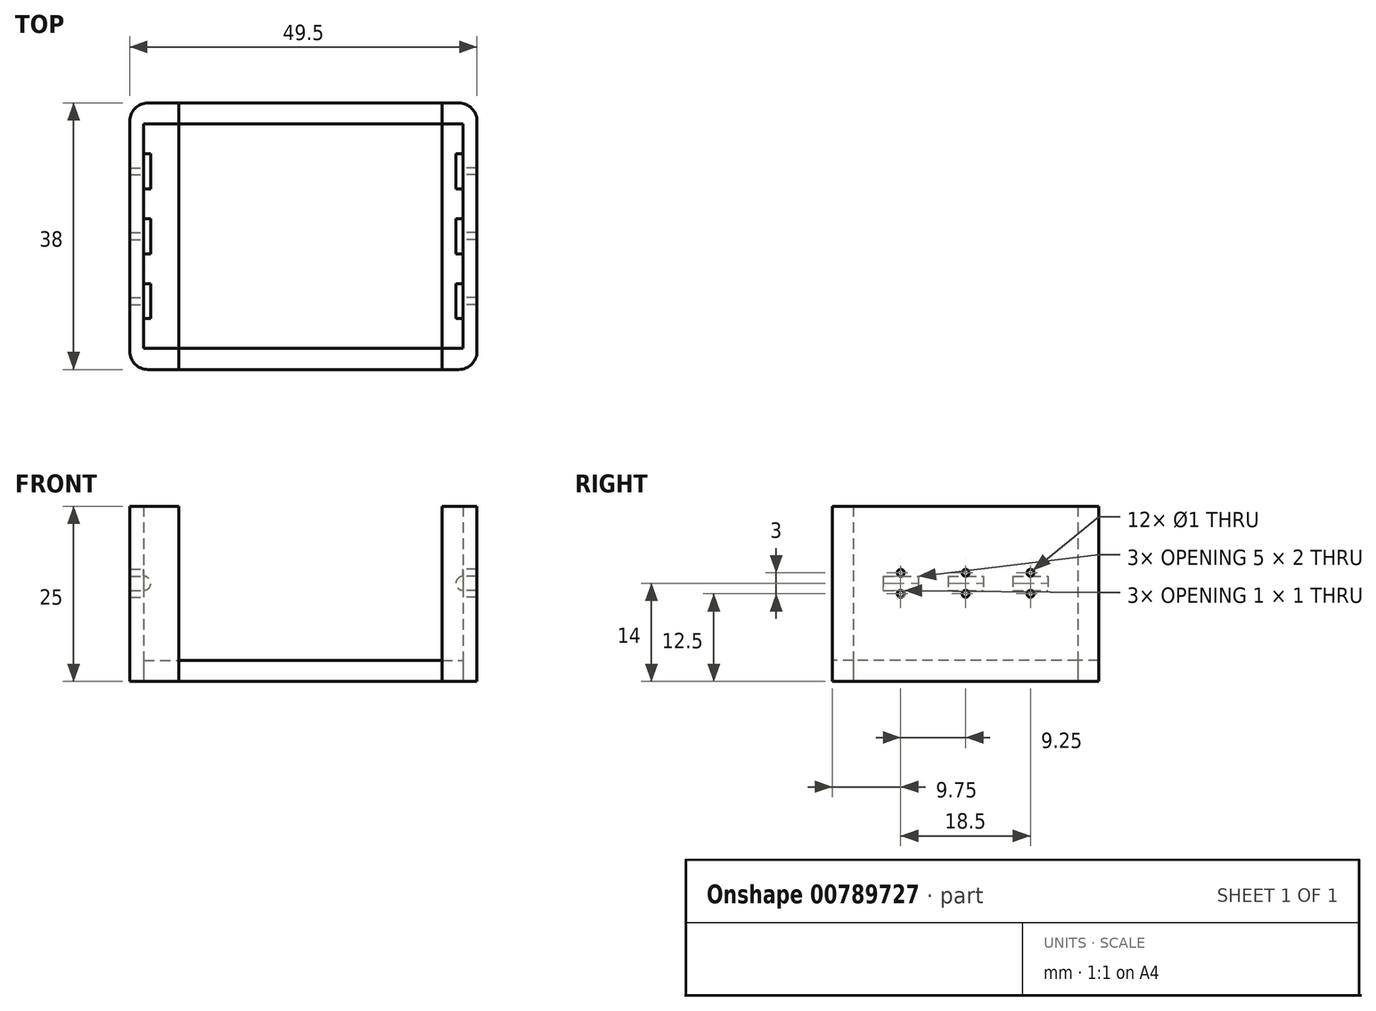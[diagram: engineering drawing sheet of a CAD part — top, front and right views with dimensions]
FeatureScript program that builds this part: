
annotation { "Feature Type Name" : "Feature", "Feature Type Description" : "" }
export const myFeature = defineFeature(function(context is Context, id is Id, definition is map)
    precondition{}
    {
        {
            var Q0;
            Q0=qCreatedBy(makeId("Top.planeOp"),FACE);
            var sketch = newSketch(context, id + "F0", { "sketchPlane" : qUnion([Q0])});
            skLineSegment(sketch, "E0.bottom", {"start": v(-24.75, 19) * mm, "end": v(24.75, 19) * mm});
            skLineSegment(sketch, "E0.top", {"start": v(-24.75, -19) * mm, "end": v(24.75, -19) * mm});
            skLineSegment(sketch, "E0.left", {"start": v(-24.75, 19) * mm, "end": v(-24.75, -19) * mm});
            skLineSegment(sketch, "E0.right", {"start": v(24.75, 19) * mm, "end": v(24.75, -19) * mm});
            skLineSegment(sketch, "E1.bottom", {"start": v(-24.75, 16) * mm, "end": v(24.75, 16) * mm});
            skLineSegment(sketch, "E1.top", {"start": v(-24.75, -16) * mm, "end": v(24.75, -16) * mm});
            skLineSegment(sketch, "E2", {"start": v(-22.75, 19) * mm, "end": v(-22.75, -19) * mm});
            skLineSegment(sketch, "E3", {"start": v(22.75, 19) * mm, "end": v(22.75, -19) * mm});
            skLineSegment(sketch, "E4", {"start": v(19.75, 19) * mm, "end": v(19.75, 16) * mm});
            skLineSegment(sketch, "E5", {"start": v(19.75, -16) * mm, "end": v(19.75, -19) * mm});
            skLineSegment(sketch, "E6", {"start": v(19.75, 16) * mm, "end": v(19.75, -16) * mm});
            skLineSegment(sketch, "E7", {"start": v(-17.75, 19) * mm, "end": v(-17.75, -19) * mm});
            skSolve(sketch);
        }
        {
            var Q0;
            {var subQ0=sQuery(id+"F0.wireOp",EDGE,"E1.bottom");var subQ1=sQuery(id+"F0.wireOp",EDGE,"E0.left");var subQ2=makeQuery(id+"F0.imprint","INTERSECT",VERTEX,{"derivedFrom":[subQ1,subQ0]});Q0=makeQuery(id+"F0.imprint","IMPRINT",FACE,{"disambiguationData":[TD([[makeQuery(id+"F0.imprint","IMPRINT",EDGE,{"disambiguationData":[TD([[subQ2,-1.0]])],"derivedFrom":subQ1}),1.0]])]});}
            var Q1;
            {var subQ0=sQuery(id+"F0.wireOp",EDGE,"E0.left");var subQ1=sQuery(id+"F0.wireOp",EDGE,"E0.bottom");var subQ2=makeQuery(id+"F0.imprint","INTERSECT",VERTEX,{"derivedFrom":[subQ1,subQ0]});Q1=makeQuery(id+"F0.imprint","IMPRINT",FACE,{"disambiguationData":[TD([[makeQuery(id+"F0.imprint","IMPRINT",EDGE,{"disambiguationData":[TD([[subQ2,-1.0]])],"derivedFrom":subQ1}),-1.0]])]});}
            var Q2;
            {var subQ3=sQuery(id+"F0.wireOp",EDGE,"JlUuSNjJ-N2WR-d7uv-6GBG-oXMLz9WUw5uQ");Q2=makeQuery(id+"F0.imprint","IMPRINT",FACE,{"disambiguationData":[TD([[makeQuery(id+"F0.imprint","IMPRINT",EDGE,{"derivedFrom":subQ3}),-1.0]])]});}
            var Q3;
            {var subQ3=sQuery(id+"F0.wireOp",EDGE,"6ny0mRPX-NTV9-We4M-mDfU-sZ6HuERO2ziz");Q3=makeQuery(id+"F0.imprint","IMPRINT",FACE,{"disambiguationData":[TD([[makeQuery(id+"F0.imprint","IMPRINT",EDGE,{"derivedFrom":subQ3}),-1.0]])]});}
            var Q4;
            {var subQ0=sQuery(id+"F0.wireOp",EDGE,"E0.left");var subQ1=sQuery(id+"F0.wireOp",EDGE,"E0.top");var subQ2=makeQuery(id+"F0.imprint","INTERSECT",VERTEX,{"derivedFrom":[subQ1,subQ0]});Q4=makeQuery(id+"F0.imprint","IMPRINT",FACE,{"disambiguationData":[TD([[makeQuery(id+"F0.imprint","IMPRINT",EDGE,{"disambiguationData":[TD([[subQ2,-1.0]])],"derivedFrom":subQ1}),1.0]])]});}
            var Q5;
            {var subQ3=sQuery(id+"F0.wireOp",EDGE,"E5");Q5=makeQuery(id+"F0.imprint","IMPRINT",FACE,{"disambiguationData":[TD([[makeQuery(id+"F0.imprint","IMPRINT",EDGE,{"derivedFrom":subQ3}),1.0]])]});}
            var Q6;
            {var subQ0=sQuery(id+"F0.wireOp",EDGE,"E0.right");var subQ1=sQuery(id+"F0.wireOp",EDGE,"E0.top");var subQ2=makeQuery(id+"F0.imprint","INTERSECT",VERTEX,{"derivedFrom":[subQ1,subQ0]});Q6=makeQuery(id+"F0.imprint","IMPRINT",FACE,{"disambiguationData":[TD([[makeQuery(id+"F0.imprint","IMPRINT",EDGE,{"disambiguationData":[TD([[subQ2,1.0]])],"derivedFrom":subQ1}),1.0]])]});}
            var Q7;
            {var subQ0=sQuery(id+"F0.wireOp",EDGE,"E1.bottom");var subQ1=sQuery(id+"F0.wireOp",EDGE,"E0.right");var subQ2=makeQuery(id+"F0.imprint","INTERSECT",VERTEX,{"derivedFrom":[subQ1,subQ0]});Q7=makeQuery(id+"F0.imprint","IMPRINT",FACE,{"disambiguationData":[TD([[makeQuery(id+"F0.imprint","IMPRINT",EDGE,{"disambiguationData":[TD([[subQ2,-1.0]])],"derivedFrom":subQ1}),-1.0]])]});}
            var Q8;
            {var subQ0=sQuery(id+"F0.wireOp",EDGE,"E0.right");var subQ1=sQuery(id+"F0.wireOp",EDGE,"E0.bottom");var subQ2=makeQuery(id+"F0.imprint","INTERSECT",VERTEX,{"derivedFrom":[subQ1,subQ0]});Q8=makeQuery(id+"F0.imprint","IMPRINT",FACE,{"disambiguationData":[TD([[makeQuery(id+"F0.imprint","IMPRINT",EDGE,{"disambiguationData":[TD([[subQ2,1.0]])],"derivedFrom":subQ1}),-1.0]])]});}
            var Q9;
            {var subQ3=sQuery(id+"F0.wireOp",EDGE,"E4");Q9=makeQuery(id+"F0.imprint","IMPRINT",FACE,{"disambiguationData":[TD([[makeQuery(id+"F0.imprint","IMPRINT",EDGE,{"derivedFrom":subQ3}),1.0]])]});}
            var Q10;
            {var subQ0=sQuery(id+"F0.wireOp",EDGE,"E2");var subQ1=sQuery(id+"F0.wireOp",EDGE,"E0.bottom");var subQ2=makeQuery(id+"F0.imprint","INTERSECT",VERTEX,{"derivedFrom":[subQ1,subQ0]});Q10=makeQuery(id+"F0.imprint","IMPRINT",FACE,{"disambiguationData":[TD([[makeQuery(id+"F0.imprint","IMPRINT",EDGE,{"disambiguationData":[TD([[subQ2,-1.0]])],"derivedFrom":subQ1}),-1.0]])]});}
            var Q11;
            {var subQ0=sQuery(id+"F0.wireOp",EDGE,"E2");var subQ1=sQuery(id+"F0.wireOp",EDGE,"E0.top");var subQ2=makeQuery(id+"F0.imprint","INTERSECT",VERTEX,{"derivedFrom":[subQ1,subQ0]});Q11=makeQuery(id+"F0.imprint","IMPRINT",FACE,{"disambiguationData":[TD([[makeQuery(id+"F0.imprint","IMPRINT",EDGE,{"disambiguationData":[TD([[subQ2,-1.0]])],"derivedFrom":subQ1}),1.0]])]});}
            extrude(context, id + "F1", {"entities" : qUnion([Q0, Q1, Q2, Q3, Q4, Q5, Q6, Q7, Q8, Q9, Q10, Q11]), "depth" : 25 * mm, "offsetDistance" : 25 * mm});
        }
        {
            var Q0;
            {var subQ0=sQuery(id+"F0.wireOp",EDGE,"JlUuSNjJ-N2WR-d7uv-6GBG-oXMLz9WUw5uQ");Q0=makeQuery(id+"F0.imprint","IMPRINT",FACE,{"disambiguationData":[TD([[makeQuery(id+"F0.imprint","IMPRINT",EDGE,{"derivedFrom":subQ0}),1.0]])]});}
            var Q1;
            {var subQ0=sQuery(id+"F0.wireOp",EDGE,"6ny0mRPX-NTV9-We4M-mDfU-sZ6HuERO2ziz");Q1=makeQuery(id+"F0.imprint","IMPRINT",FACE,{"disambiguationData":[TD([[makeQuery(id+"F0.imprint","IMPRINT",EDGE,{"derivedFrom":subQ0}),1.0]])]});}
            var Q2;
            {var subQ0=sQuery(id+"F0.wireOp",EDGE,"7H7hESgq-7wWA-rG7u-VLva-y2kTmdD04vns");Q2=makeQuery(id+"F0.imprint","IMPRINT",FACE,{"disambiguationData":[TD([[makeQuery(id+"F0.imprint","IMPRINT",EDGE,{"derivedFrom":subQ0}),1.0]])]});}
            var Q3;
            {var subQ0=sQuery(id+"F0.wireOp",EDGE,"E6");Q3=makeQuery(id+"F0.imprint","IMPRINT",FACE,{"disambiguationData":[TD([[makeQuery(id+"F0.imprint","IMPRINT",EDGE,{"derivedFrom":subQ0}),1.0]])]});}
            var Q4;
            {var subQ2=sQuery(id+"F0.wireOp",EDGE,"kKINSNnD-868z-kQwc-rezc-MHWNEOe5RiWT");Q4=makeQuery(id+"F0.imprint","IMPRINT",FACE,{"disambiguationData":[TD([[makeQuery(id+"F0.imprint","IMPRINT",EDGE,{"derivedFrom":subQ2}),-1.0]])]});}
            var Q5;
            {var subQ0=sQuery(id+"F0.wireOp",EDGE,"E4");Q5=makeQuery(id+"F0.imprint","IMPRINT",FACE,{"disambiguationData":[TD([[makeQuery(id+"F0.imprint","IMPRINT",EDGE,{"derivedFrom":subQ0}),-1.0]])]});}
            var Q6;
            {var subQ0=sQuery(id+"F0.wireOp",EDGE,"E2");var subQ1=sQuery(id+"F0.wireOp",EDGE,"E1.bottom");var subQ2=makeQuery(id+"F0.imprint","INTERSECT",VERTEX,{"derivedFrom":[subQ1,subQ0]});Q6=makeQuery(id+"F0.imprint","IMPRINT",FACE,{"disambiguationData":[TD([[makeQuery(id+"F0.imprint","IMPRINT",EDGE,{"disambiguationData":[TD([[subQ2,-1.0]])],"derivedFrom":subQ1}),-1.0]])]});}
            var Q7;
            {var subQ0=sQuery(id+"F0.wireOp",EDGE,"E5");Q7=makeQuery(id+"F0.imprint","IMPRINT",FACE,{"disambiguationData":[TD([[makeQuery(id+"F0.imprint","IMPRINT",EDGE,{"derivedFrom":subQ0}),-1.0]])]});}
            extrude(context, id + "F2", {"entities" : qUnion([Q0, Q1, Q2, Q3, Q4, Q5, Q6, Q7]), "depth" : 3 * mm, "offsetDistance" : 25 * mm});
        }
        {
            var Q0;
            Q0=makeQuery(id+"F1.opExtrude","SWEPT_EDGE",EDGE,{"disambiguationData":[OSD([sQuery(id+"F0.wireOp",EDGE,"E0.bottom"),sQuery(id+"F0.wireOp",EDGE,"E0.left")])]});
            var Q1;
            Q1=makeQuery(id+"F1.opExtrude","SWEPT_EDGE",EDGE,{"disambiguationData":[OSD([sQuery(id+"F0.wireOp",EDGE,"E0.bottom"),sQuery(id+"F0.wireOp",EDGE,"E0.right")])]});
            var Q2;
            Q2=makeQuery(id+"F1.opExtrude","SWEPT_EDGE",EDGE,{"disambiguationData":[OSD([sQuery(id+"F0.wireOp",EDGE,"E0.top"),sQuery(id+"F0.wireOp",EDGE,"E0.right")])]});
            var Q3;
            Q3=makeQuery(id+"F1.opExtrude","SWEPT_EDGE",EDGE,{"disambiguationData":[OSD([sQuery(id+"F0.wireOp",EDGE,"E0.top"),sQuery(id+"F0.wireOp",EDGE,"E0.left")])]});
            fillet(context, id + "F3", {"entities" : qUnion([Q0, Q1, Q2, Q3]), "radius" : 2.6 * mm, "tangentPropagation" : true, "allowEdgeOverflow" : false});
        }
        {
            var Q0;
            Q0=makeQuery(id+"F1.opExtrude","CAP_EDGE",EDGE,{"disambiguationData":[OSD([sQuery(id+"F0.wireOp",EDGE,"E3")])],"isStart":false});
            cPlane(context, id + "F4", {"entities" : qUnion([Q0]), "cplaneType" : CPlaneType.LINE_ANGLE, "offset" : 25 * mm, "angle" : 90 * degree, "width" : 150 * mm, "height" : 150 * mm});
        }
        {
            var Q0;
            Q0=qCreatedBy(id+"F4.planeOp",FACE);
            var sketch = newSketch(context, id + "F5", { "sketchPlane" : qUnion([Q0])});
            skLineSegment(sketch, "E8.bottom", {"start": v(-16, 25) * mm, "end": v(16, 25) * mm});
            skLineSegment(sketch, "E8.top", {"start": v(-16, 3) * mm, "end": v(16, 3) * mm});
            skLineSegment(sketch, "E8.left", {"start": v(-16, 25) * mm, "end": v(-16, 3) * mm});
            skLineSegment(sketch, "E8.right", {"start": v(16, 25) * mm, "end": v(16, 3) * mm});
            skLineSegment(sketch, "E9.bottom", {"start": v(-11.75, 13) * mm, "end": v(-6.75, 13) * mm});
            skLineSegment(sketch, "E9.top", {"start": v(-11.75, 15) * mm, "end": v(-6.75, 15) * mm});
            skLineSegment(sketch, "E9.left", {"start": v(-11.75, 15) * mm, "end": v(-11.75, 13) * mm});
            skLineSegment(sketch, "E9.right", {"start": v(-6.75, 15) * mm, "end": v(-6.75, 13) * mm});
            skLineSegment(sketch, "E10.bottom", {"start": v(-2.5, 13) * mm, "end": v(2.5, 13) * mm});
            skLineSegment(sketch, "E10.top", {"start": v(-2.5, 15) * mm, "end": v(2.5, 15) * mm});
            skLineSegment(sketch, "E10.left", {"start": v(-2.5, 15) * mm, "end": v(-2.5, 13) * mm});
            skLineSegment(sketch, "E10.right", {"start": v(2.5, 15) * mm, "end": v(2.5, 13) * mm});
            skLineSegment(sketch, "E11.bottom", {"start": v(6.75, 13) * mm, "end": v(11.75, 13) * mm});
            skLineSegment(sketch, "E11.top", {"start": v(6.75, 15) * mm, "end": v(11.75, 15) * mm});
            skLineSegment(sketch, "E11.left", {"start": v(6.75, 15) * mm, "end": v(6.75, 13) * mm});
            skLineSegment(sketch, "E11.right", {"start": v(11.75, 15) * mm, "end": v(11.75, 13) * mm});
            skLineSegment(sketch, "E12", {"start": v(11.75, 14) * mm, "end": v(16, 14) * mm, "construction": true});
            skLineSegment(sketch, "E13", {"start": v(-11.75, 14) * mm, "end": v(-16, 14) * mm, "construction": true});
            skLineSegment(sketch, "E14", {"start": v(-6.75, 14) * mm, "end": v(-2.5, 14) * mm, "construction": true});
            skLineSegment(sketch, "E15", {"start": v(2.5, 14) * mm, "end": v(6.75, 14) * mm, "construction": true});
            skCircle(sketch, "E16", {"center": v(-9.25, 15.5) * mm, "radius": 0.5 * mm});
            skPoint(sketch, "E16.centerSnap0", {"position": v(-9.25, 15) * mm});
            skCircle(sketch, "E17", {"center": v(0, 15.5) * mm, "radius": 0.5 * mm});
            skPoint(sketch, "E17.centerSnap0", {"position": v(0, 15) * mm});
            skCircle(sketch, "E18", {"center": v(9.25, 15.5) * mm, "radius": 0.5 * mm});
            skPoint(sketch, "E18.centerSnap0", {"position": v(9.25, 15) * mm});
            skCircle(sketch, "E19", {"center": v(-9.25, 12.5) * mm, "radius": 0.5 * mm});
            skPoint(sketch, "E19.centerSnap0", {"position": v(-9.25, 13) * mm});
            skCircle(sketch, "E20", {"center": v(0, 12.5) * mm, "radius": 0.5 * mm});
            skPoint(sketch, "E20.centerSnap0", {"position": v(0, 13) * mm});
            skCircle(sketch, "E21", {"center": v(9.25, 12.5) * mm, "radius": 0.5 * mm});
            skPoint(sketch, "E21.centerSnap0", {"position": v(9.25, 13) * mm});
            skSolve(sketch);
        }
        {
            var Q0;
            Q0=makeQuery(id+"F5.imprint","IMPRINT",FACE,{"disambiguationData":[TD([[makeQuery(id+"F5.imprint","IMPRINT",EDGE,{"derivedFrom":sQuery(id+"F5.wireOp",EDGE,"E9.bottom")}),1.0]])]});
            var Q1;
            Q1=makeQuery(id+"F5.imprint","IMPRINT",FACE,{"disambiguationData":[TD([[makeQuery(id+"F5.imprint","IMPRINT",EDGE,{"derivedFrom":sQuery(id+"F5.wireOp",EDGE,"E10.bottom")}),1.0]])]});
            var Q2;
            Q2=makeQuery(id+"F5.imprint","IMPRINT",FACE,{"disambiguationData":[TD([[makeQuery(id+"F5.imprint","IMPRINT",EDGE,{"derivedFrom":sQuery(id+"F5.wireOp",EDGE,"E11.bottom")}),1.0]])]});
            extrude(context, id + "F6", {"entities" : qUnion([Q0, Q1, Q2]), "operationType" : NewBodyOperationType.ADD, "oppositeDirection" : true, "depth" : 1 * mm, "offsetDistance" : 25 * mm});
        }
        {
            var Q0;
            Q0=makeQuery(id+"F6.opExtrude","CAP_EDGE",EDGE,{"disambiguationData":[OSD([sQuery(id+"F5.wireOp",EDGE,"E9.top")])],"isStart":false});
            var Q1;
            Q1=makeQuery(id+"F6.opExtrude","CAP_EDGE",EDGE,{"disambiguationData":[OSD([sQuery(id+"F5.wireOp",EDGE,"E9.bottom")])],"isStart":false});
            var Q2;
            Q2=makeQuery(id+"F6.opExtrude","CAP_EDGE",EDGE,{"disambiguationData":[OSD([sQuery(id+"F5.wireOp",EDGE,"E10.top")])],"isStart":false});
            var Q3;
            Q3=makeQuery(id+"F6.opExtrude","CAP_EDGE",EDGE,{"disambiguationData":[OSD([sQuery(id+"F5.wireOp",EDGE,"E10.bottom")])],"isStart":false});
            var Q4;
            Q4=makeQuery(id+"F6.opExtrude","CAP_EDGE",EDGE,{"disambiguationData":[OSD([sQuery(id+"F5.wireOp",EDGE,"E11.bottom")])],"isStart":false});
            var Q5;
            Q5=makeQuery(id+"F6.opExtrude","CAP_EDGE",EDGE,{"disambiguationData":[OSD([sQuery(id+"F5.wireOp",EDGE,"E11.top")])],"isStart":false});
            fillet(context, id + "F7", {"entities" : qUnion([Q0, Q1, Q2, Q3, Q4, Q5]), "radius" : 1 * mm, "tangentPropagation" : true, "allowEdgeOverflow" : false});
        }
        {
            var Q0;
            Q0=makeQuery(id+"F1.opExtrude","CAP_EDGE",EDGE,{"disambiguationData":[OSD([sQuery(id+"F0.wireOp",EDGE,"E2")])],"isStart":false});
            cPlane(context, id + "F8", {"entities" : qUnion([Q0]), "cplaneType" : CPlaneType.LINE_ANGLE, "offset" : 25 * mm, "angle" : 90 * degree, "width" : 150 * mm, "height" : 150 * mm});
        }
        {
            var Q0;
            Q0=qCreatedBy(id+"F8.planeOp",FACE);
            var sketch = newSketch(context, id + "F9", { "sketchPlane" : qUnion([Q0])});
            skLineSegment(sketch, "E22.bottom", {"start": v(-16, 25) * mm, "end": v(16, 25) * mm});
            skLineSegment(sketch, "E22.top", {"start": v(-16, 3) * mm, "end": v(16, 3) * mm});
            skLineSegment(sketch, "E22.left", {"start": v(-16, 25) * mm, "end": v(-16, 3) * mm});
            skLineSegment(sketch, "E22.right", {"start": v(16, 25) * mm, "end": v(16, 3) * mm});
            skLineSegment(sketch, "E23.bottom", {"start": v(-11.75, 13) * mm, "end": v(-6.75, 13) * mm});
            skLineSegment(sketch, "E23.top", {"start": v(-11.75, 15) * mm, "end": v(-6.75, 15) * mm});
            skLineSegment(sketch, "E23.left", {"start": v(-11.75, 15) * mm, "end": v(-11.75, 13) * mm});
            skLineSegment(sketch, "E23.right", {"start": v(-6.75, 15) * mm, "end": v(-6.75, 13) * mm});
            skLineSegment(sketch, "E24.bottom", {"start": v(-2.5, 13) * mm, "end": v(2.5, 13) * mm});
            skLineSegment(sketch, "E24.top", {"start": v(-2.5, 15) * mm, "end": v(2.5, 15) * mm});
            skLineSegment(sketch, "E24.left", {"start": v(-2.5, 15) * mm, "end": v(-2.5, 13) * mm});
            skLineSegment(sketch, "E24.right", {"start": v(2.5, 15) * mm, "end": v(2.5, 13) * mm});
            skLineSegment(sketch, "E25.bottom", {"start": v(6.75, 13) * mm, "end": v(11.75, 13) * mm});
            skLineSegment(sketch, "E25.top", {"start": v(6.75, 15) * mm, "end": v(11.75, 15) * mm});
            skLineSegment(sketch, "E25.left", {"start": v(6.75, 15) * mm, "end": v(6.75, 13) * mm});
            skLineSegment(sketch, "E25.right", {"start": v(11.75, 15) * mm, "end": v(11.75, 13) * mm});
            skLineSegment(sketch, "E26", {"start": v(11.75, 14) * mm, "end": v(16, 14) * mm, "construction": true});
            skLineSegment(sketch, "E27", {"start": v(-11.75, 14) * mm, "end": v(-16, 14) * mm, "construction": true});
            skLineSegment(sketch, "E28", {"start": v(-6.75, 14) * mm, "end": v(-2.5, 14) * mm, "construction": true});
            skLineSegment(sketch, "E29", {"start": v(2.5, 14) * mm, "end": v(6.75, 14) * mm, "construction": true});
            skCircle(sketch, "E30", {"center": v(9.25, 15.5) * mm, "radius": 0.5 * mm});
            skPoint(sketch, "E30.centerSnap0", {"position": v(9.25, 15) * mm});
            skCircle(sketch, "E31", {"center": v(0, 15.5) * mm, "radius": 0.5 * mm});
            skCircle(sketch, "E32", {"center": v(-9.25, 15.5) * mm, "radius": 0.5 * mm});
            skPoint(sketch, "E32.centerSnap0", {"position": v(-9.25, 15) * mm});
            skCircle(sketch, "E33", {"center": v(-9.25, 12.5) * mm, "radius": 0.5 * mm});
            skPoint(sketch, "E33.centerSnap0", {"position": v(-9.25, 13) * mm});
            skCircle(sketch, "E34", {"center": v(0, 12.5) * mm, "radius": 0.5 * mm});
            skPoint(sketch, "E34.centerSnap0", {"position": v(0, 13) * mm});
            skCircle(sketch, "E35", {"center": v(9.25, 12.5) * mm, "radius": 0.5 * mm});
            skPoint(sketch, "E35.centerSnap0", {"position": v(9.25, 13) * mm});
            skSolve(sketch);
        }
        {
            var Q0;
            Q0=makeQuery(id+"F9.imprint","IMPRINT",FACE,{"disambiguationData":[TD([[makeQuery(id+"F9.imprint","IMPRINT",EDGE,{"derivedFrom":sQuery(id+"F9.wireOp",EDGE,"E23.bottom")}),1.0]])]});
            var Q1;
            Q1=makeQuery(id+"F9.imprint","IMPRINT",FACE,{"disambiguationData":[TD([[makeQuery(id+"F9.imprint","IMPRINT",EDGE,{"derivedFrom":sQuery(id+"F9.wireOp",EDGE,"E24.bottom")}),1.0]])]});
            var Q2;
            Q2=makeQuery(id+"F9.imprint","IMPRINT",FACE,{"disambiguationData":[TD([[makeQuery(id+"F9.imprint","IMPRINT",EDGE,{"derivedFrom":sQuery(id+"F9.wireOp",EDGE,"E25.bottom")}),1.0]])]});
            extrude(context, id + "F10", {"entities" : qUnion([Q0, Q1, Q2]), "operationType" : NewBodyOperationType.ADD, "depth" : 1 * mm, "offsetDistance" : 25 * mm});
        }
        {
            var Q0;
            Q0=makeQuery(id+"F10.opExtrude","CAP_EDGE",EDGE,{"disambiguationData":[OSD([sQuery(id+"F9.wireOp",EDGE,"E23.top")])],"isStart":false});
            var Q1;
            Q1=makeQuery(id+"F10.opExtrude","CAP_EDGE",EDGE,{"disambiguationData":[OSD([sQuery(id+"F9.wireOp",EDGE,"E23.bottom")])],"isStart":false});
            var Q2;
            Q2=makeQuery(id+"F10.opExtrude","CAP_EDGE",EDGE,{"disambiguationData":[OSD([sQuery(id+"F9.wireOp",EDGE,"E24.top")])],"isStart":false});
            var Q3;
            Q3=makeQuery(id+"F10.opExtrude","CAP_EDGE",EDGE,{"disambiguationData":[OSD([sQuery(id+"F9.wireOp",EDGE,"E25.top")])],"isStart":false});
            var Q4;
            Q4=makeQuery(id+"F10.opExtrude","CAP_EDGE",EDGE,{"disambiguationData":[OSD([sQuery(id+"F9.wireOp",EDGE,"E24.bottom")])],"isStart":false});
            var Q5;
            Q5=makeQuery(id+"F10.opExtrude","CAP_EDGE",EDGE,{"disambiguationData":[OSD([sQuery(id+"F9.wireOp",EDGE,"E25.bottom")])],"isStart":false});
            fillet(context, id + "F11", {"entities" : qUnion([Q0, Q1, Q2, Q3, Q4, Q5]), "radius" : 1 * mm, "tangentPropagation" : true, "allowEdgeOverflow" : false});
        }
        {
            var Q0;
            Q0=makeQuery(id+"F5.imprint","IMPRINT",FACE,{"disambiguationData":[TD([[makeQuery(id+"F5.imprint","IMPRINT",EDGE,{"derivedFrom":sQuery(id+"F5.wireOp",EDGE,"E16")}),1.0]])]});
            var Q1;
            Q1=makeQuery(id+"F5.imprint","IMPRINT",FACE,{"disambiguationData":[TD([[makeQuery(id+"F5.imprint","IMPRINT",EDGE,{"derivedFrom":sQuery(id+"F5.wireOp",EDGE,"E17")}),1.0]])]});
            var Q2;
            Q2=makeQuery(id+"F5.imprint","IMPRINT",FACE,{"disambiguationData":[TD([[makeQuery(id+"F5.imprint","IMPRINT",EDGE,{"derivedFrom":sQuery(id+"F5.wireOp",EDGE,"E18")}),1.0]])]});
            var Q3;
            Q3=makeQuery(id+"F5.imprint","IMPRINT",FACE,{"disambiguationData":[TD([[makeQuery(id+"F5.imprint","IMPRINT",EDGE,{"derivedFrom":sQuery(id+"F5.wireOp",EDGE,"E21")}),1.0]])]});
            var Q4;
            Q4=makeQuery(id+"F5.imprint","IMPRINT",FACE,{"disambiguationData":[TD([[makeQuery(id+"F5.imprint","IMPRINT",EDGE,{"derivedFrom":sQuery(id+"F5.wireOp",EDGE,"E20")}),1.0]])]});
            var Q5;
            Q5=makeQuery(id+"F5.imprint","IMPRINT",FACE,{"disambiguationData":[TD([[makeQuery(id+"F5.imprint","IMPRINT",EDGE,{"derivedFrom":sQuery(id+"F5.wireOp",EDGE,"E19")}),1.0]])]});
            extrude(context, id + "F12", {"entities" : qUnion([Q0, Q1, Q2, Q3, Q4, Q5]), "operationType" : NewBodyOperationType.REMOVE, "depth" : 5 * mm, "offsetDistance" : 25 * mm});
        }
        {
            var Q0;
            Q0=makeQuery(id+"F9.imprint","IMPRINT",FACE,{"disambiguationData":[TD([[makeQuery(id+"F9.imprint","IMPRINT",EDGE,{"derivedFrom":sQuery(id+"F9.wireOp",EDGE,"E32")}),1.0]])]});
            var Q1;
            Q1=makeQuery(id+"F9.imprint","IMPRINT",FACE,{"disambiguationData":[TD([[makeQuery(id+"F9.imprint","IMPRINT",EDGE,{"derivedFrom":sQuery(id+"F9.wireOp",EDGE,"E31")}),1.0]])]});
            var Q2;
            Q2=makeQuery(id+"F9.imprint","IMPRINT",FACE,{"disambiguationData":[TD([[makeQuery(id+"F9.imprint","IMPRINT",EDGE,{"derivedFrom":sQuery(id+"F9.wireOp",EDGE,"E30")}),1.0]])]});
            var Q3;
            Q3=makeQuery(id+"F9.imprint","IMPRINT",FACE,{"disambiguationData":[TD([[makeQuery(id+"F9.imprint","IMPRINT",EDGE,{"derivedFrom":sQuery(id+"F9.wireOp",EDGE,"E35")}),1.0]])]});
            var Q4;
            Q4=makeQuery(id+"F9.imprint","IMPRINT",FACE,{"disambiguationData":[TD([[makeQuery(id+"F9.imprint","IMPRINT",EDGE,{"derivedFrom":sQuery(id+"F9.wireOp",EDGE,"E34")}),1.0]])]});
            var Q5;
            Q5=makeQuery(id+"F9.imprint","IMPRINT",FACE,{"disambiguationData":[TD([[makeQuery(id+"F9.imprint","IMPRINT",EDGE,{"derivedFrom":sQuery(id+"F9.wireOp",EDGE,"E33")}),1.0]])]});
            extrude(context, id + "F13", {"entities" : qUnion([Q0, Q1, Q2, Q3, Q4, Q5]), "operationType" : NewBodyOperationType.REMOVE, "oppositeDirection" : true, "depth" : 5 * mm, "offsetDistance" : 25 * mm});
        }
    });
